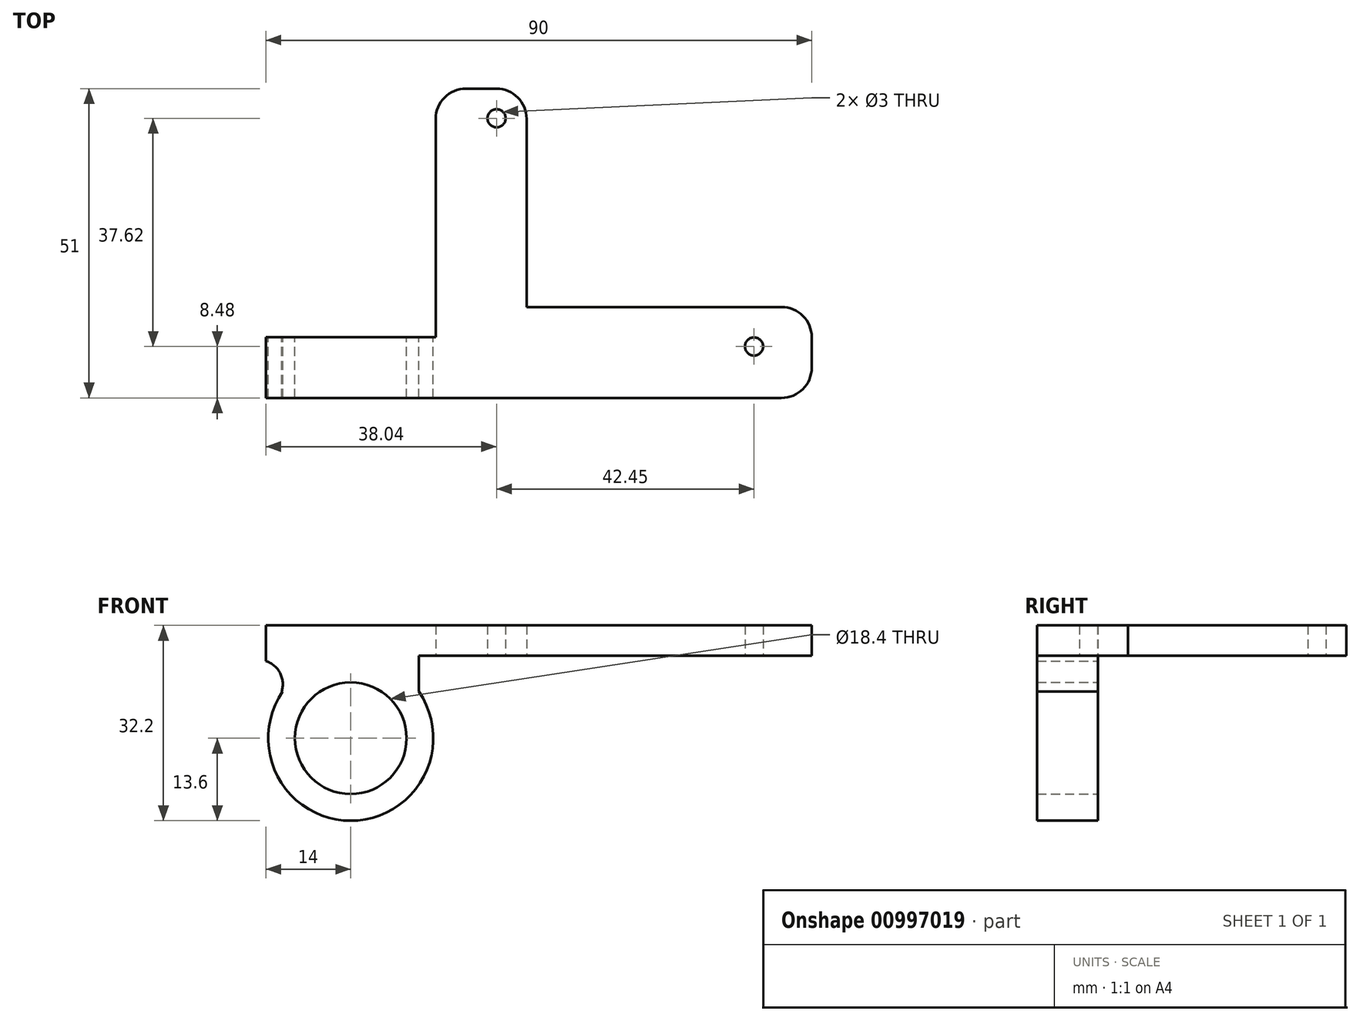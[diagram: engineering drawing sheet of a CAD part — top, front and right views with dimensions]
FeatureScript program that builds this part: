
annotation { "Feature Type Name" : "Feature", "Feature Type Description" : "" }
export const myFeature = defineFeature(function(context is Context, id is Id, definition is map)
    precondition{}
    {
        {
            var Q0;
            Q0=qCreatedBy(makeId("Top.planeOp"),FACE);
            var sketch = newSketch(context, id + "F0", { "sketchPlane" : qUnion([Q0])});
            skLineSegment(sketch, "E0.bottom", {"start": v(-5, 0) * mm, "end": v(-62, 0) * mm});
            skLineSegment(sketch, "E0.top", {"start": v(-52, 51) * mm, "end": v(-57, 51) * mm});
            skLineSegment(sketch, "E0.left", {"start": v(0, 5) * mm, "end": v(0, 10) * mm});
            skLineSegment(sketch, "E0.right", {"start": v(-62, 0) * mm, "end": v(-62, 46) * mm});
            skLineSegment(sketch, "E1.bottom", {"start": v(-90, 10) * mm, "end": v(-62, 10) * mm});
            skLineSegment(sketch, "E1.top", {"start": v(-90, 0) * mm, "end": v(-62, 0) * mm});
            skLineSegment(sketch, "E1.left", {"start": v(-90, 10) * mm, "end": v(-90, 0) * mm});
            skLineSegment(sketch, "E1.right", {"start": v(-62, 10) * mm, "end": v(-62, 0) * mm});
            skCircle(sketch, "E2", {"center": v(-51.96, 46.1) * mm, "radius": 1.5 * mm});
            skCircle(sketch, "E3", {"center": v(-9.51, 8.48) * mm, "radius": 1.5 * mm});
            skLineSegment(sketch, "E4.top", {"start": v(-62, 0) * mm, "end": v(-15, 0) * mm});
            skLineSegment(sketch, "E4.left", {"start": v(-62, 41) * mm, "end": v(-62, 0) * mm});
            skLineSegment(sketch, "E5.top", {"start": v(-47, 15) * mm, "end": v(-5, 15) * mm});
            skLineSegment(sketch, "E5.left", {"start": v(-47, 46) * mm, "end": v(-47, 15) * mm});
            skPoint(sketch, "E6.visualSharp", {"position": v(-47, 51) * mm});
            skArc(sketch, "E6.filletArc", {"start": v(-47, 46) * mm, "mid": v(-48.46, 49.54) * mm, "end": v(-52, 51) * mm});
            skPoint(sketch, "E7.visualSharp", {"position": v(0, 15) * mm});
            skArc(sketch, "E7.filletArc", {"start": v(0, 10) * mm, "mid": v(-1.46, 13.54) * mm, "end": v(-5, 15) * mm});
            skPoint(sketch, "E8.visualSharp", {"position": v(0, 0) * mm});
            skArc(sketch, "E8.filletArc", {"start": v(-5, 0) * mm, "mid": v(-1.46, 1.46) * mm, "end": v(0, 5) * mm});
            skPoint(sketch, "E9.visualSharp", {"position": v(-62, 51) * mm});
            skArc(sketch, "E9.filletArc", {"start": v(-57, 51) * mm, "mid": v(-60.54, 49.54) * mm, "end": v(-62, 46) * mm});
            skSolve(sketch);
        }
        {
            var Q0;
            Q0=makeQuery(id+"F0.imprint","IMPRINT",FACE,{"disambiguationData":[TD([[makeQuery(id+"F0.imprint","IMPRINT",EDGE,{"derivedFrom":sQuery(id+"F0.wireOp",EDGE,"E0.bottom")}),-1.0]])]});
            var Q1;
            {var subQ0=sQuery(id+"F0.wireOp",EDGE,"E1.bottom");Q1=makeQuery(id+"F0.imprint","IMPRINT",FACE,{"disambiguationData":[TD([[makeQuery(id+"F0.imprint","IMPRINT",EDGE,{"derivedFrom":subQ0}),-1.0]])]});}
            extrude(context, id + "F1", {"entities" : qUnion([Q0, Q1]), "depth" : 5 * mm, "offsetDistance" : 25 * mm});
        }
        {
            var Q0;
            Q0=makeQuery(id+"F1.opExtrude","SWEPT_FACE",FACE,{"disambiguationData":[OSD([sQuery(id+"F0.wireOp",EDGE,"E1.bottom")])]});
            var sketch = newSketch(context, id + "F2", { "sketchPlane" : qUnion([Q0])});
            skCircle(sketch, "E10", {"center": v(76, -13.6) * mm, "radius": 13.6 * mm});
            skPoint(sketch, "E10.centerSnap0", {"position": v(76, 0) * mm});
            skCircle(sketch, "E11", {"center": v(76, -13.6) * mm, "radius": 9.2 * mm});
            skLineSegment(sketch, "E12.bottom", {"start": v(90, 0) * mm, "end": v(64.77, 0) * mm});
            skLineSegment(sketch, "E12.top", {"start": v(87.4, -5.93) * mm, "end": v(87.23, -5.93) * mm});
            skLineSegment(sketch, "E12.left", {"start": v(90, 0) * mm, "end": v(90, -0.86) * mm});
            skLineSegment(sketch, "E12.right", {"start": v(64.77, 0) * mm, "end": v(64.77, -5.93) * mm});
            skCircle(sketch, "E13", {"center": v(91.22, -4.7) * mm, "radius": 4.02 * mm});
            skPoint(sketch, "E14.orphan", {"position": v(90, -5.93) * mm});
            skSolve(sketch);
        }
        {
            var Q0;
            {var subQ0=sQuery(id+"F2.wireOp",EDGE,"E12.right");Q0=makeQuery(id+"F2.imprint","IMPRINT",FACE,{"disambiguationData":[TD([[makeQuery(id+"F2.imprint","IMPRINT",EDGE,{"derivedFrom":subQ0}),1.0]])]});}
            var Q1;
            Q1=makeQuery(id+"F2.imprint","IMPRINT",FACE,{"disambiguationData":[TD([[makeQuery(id+"F2.imprint","IMPRINT",EDGE,{"derivedFrom":sQuery(id+"F2.wireOp",EDGE,"E11")}),-1.0]])]});
            var Q2;
            {var subQ5=sQuery(id+"F2.wireOp",EDGE,"E12.top");var subQ6=sQuery(id+"F2.wireOp",EDGE,"E10");var subQ7=makeQuery(id+"F2.imprint","INTERSECT",VERTEX,{"derivedFrom":[subQ6,subQ5]});Q2=makeQuery(id+"F2.imprint","IMPRINT",FACE,{"disambiguationData":[TD([[makeQuery(id+"F2.imprint","IMPRINT",EDGE,{"disambiguationData":[TD([[subQ7,-1.0]])],"derivedFrom":subQ6}),-1.0]])]});}
            extrude(context, id + "F3", {"entities" : qUnion([Q0, Q1, Q2]), "operationType" : NewBodyOperationType.ADD, "oppositeDirection" : true, "depth" : 10 * mm, "offsetDistance" : 25 * mm});
        }
    });
